# Revit family: Domotics-SerieCivili-GEWISS-27COMBI_SYSTEM-IP55_SPIE_SEGNALAZIONE
name_source: partatom
category: Modelli generici
revit_build: Autodesk Revit 2016 (Build: 20161004_0715(x64)
units: mm (PartAtom-declared; Revit-internal decimal feet)

## family parameters
Condiviso = No
Host = Muro
Punto di calcolo locali = No
Può ospitare armatura = No
Quota connettore circolare = Usa diametro
Sempre verticale = Sì
Taglio con vuoti quando caricato = No
Tipo di parte = Normale

## types (5) — shared parameters
Catalogo = DOMOTICS
Catalogo Serie = 27COMBI
Classe isolamento = II
Codice Electrocod = 0132
Colore = Grigio RAL 7035
Colore diffusore = GEWISS VETRINO AZZURRO
Dim. esterne BxHxP (mm) = 66x82x95
Glow Wire Test = 650°C
Grado di protezione = IP55
IDF = fbbf1421-415d-4e21-9c1b-b3b5078e022a
IDT = 7b0adaca-5341-4719-835f-f8f4d184b5d8
Immagine tipo = GW27419.jpg
Norma di riferimento = EN 60598-1
Portalampada tipo = E14
Potenza = Max 15 W
Produttore = GEWISS S.p.A.
Scheda Tecnica = https://www.gewiss.com
Temperatura di installazione = -25 +60 °C
Tensione nominale = 230 V ac
Termopressione con biglia = 70 °C
URL = https://www.gewiss.com
Versione file RFA = 18.0

## per-type parameters (varying)
| type | Codice EAN | Colore del diffusore | Descrizione | Modello |
| GW27415 - Spia segnalazione diffusore rosso stagna | 8011564056176 | Rosso | SPIA SEGNALAZ.DIFF.ROSSO STAGNA | GW27415 |
| GW27419 - Spia segnalazione diffusore azzurro stagna | 8011564056213 | Azzurro | SPIA SEGNALAZ.DIFF.AZZURRO STAGNA | GW27419 |
| GW27417 - Spia segnalazione diffusore giallo stagna | 8011564056190 | Giallo | SPIA SEGNALAZ.DIFF.GIALLO STAGNA | GW27417 |
| GW27418 - Spia segnalazione diffusore trasparente stagna | 8011564056206 | Trasparente | SPIA SEGNALAZ.DIFF.TRASPARENTE STAGNA | GW27418 |
| GW27416 - Spia segnalazione diffusore verde stagna | 8011564056183 | Verde | SPIA SEGNALAZ.DIFF.VERDE STAGNA | GW27416 |
